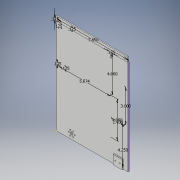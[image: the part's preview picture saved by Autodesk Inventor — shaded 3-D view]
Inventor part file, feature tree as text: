
AUTODESK INVENTOR PART (.ipt)
format: ipt  version: 2017 (Build 210142000, 142)  size: 188,416 bytes
history: native  units: in
note: dims shown in document units (in); Inventor stores cm internally (conversion verified against a paired STEP export)
features: sketch x8, extrude x4, hole x2, projected_geometry x1
ambient origin geometry x8: Origin, YZ Plane, XZ Plane, XY Plane, X Axis, Y Axis, Z Axis, Center Point
bodies: Solid1 (feature_tree)
feature tree (15):
  sketch  "Sketch1"  dims[d0=7.85in d2=0.125in]
  extrude  "Extrusion1"  Depth=0.125in
  extrude  "Extrusion2"  Depth=0.125in
  hole  "Hole1"  [1 undecoded]
  extrude  "Extrusion3"  Depth=0.125in
  sketch  "Sketch6"  dims[d11=4.25in d12=0.125in]
  extrude  "Extrusion4"  Depth=3.6in
  hole  "Hole2"  [1 undecoded]
  sketch  "Sketch2"  dims[d3=0.125in d4=5.674in]
  sketch  "Sketch3"  dims[d5=4.0in d6=0.125in]
  sketch  "Sketch4"  dims[d7=4.0in d8=0.125in]
  sketch  "Sketch5"  dims[d9=1.4in d10=3.6in]
  sketch  "Sketch7"  dims[d13=0.125in]
  sketch  "Sketch8"  dims[d14=0.125in d15=0.0in d16=0.575in d18=1.674in d19=0.0in d20=0.63in d21=0.275in d22=0.125in d23=0.25in d24=0.0in d25=2.3622in d27=360.0deg d29=0.75in d30=0.0in d31=0.5in d32=90.0deg d33=0.5in d34=0.138in d35=0.138in d36=0.104in d37=0.276in d38=0.375in d39=0.25in d40=0.5635in d41=0.432in d42=0.8108in d43=0.25in d44=0.25in d45=1.0in d46=0.125in d47=0.0in d48=0.0in d49=0.5in d50=0.0in d51=0.125in d52=0.0in d53=0.25in d54=0.25in d55=0.25in d56=0.25in d57=0.25in d58=0.75in d59=0.375in d60=0.25in d61=0.5635in d62=1.0in d63=0.8108in]
  projected_geometry  "Projected Loop1"
note: 2 required parameter values undecoded (feature->parameter linkage not recoverable at this tier; creation-order binding heuristic only, values carry confidence <= 0.55)
